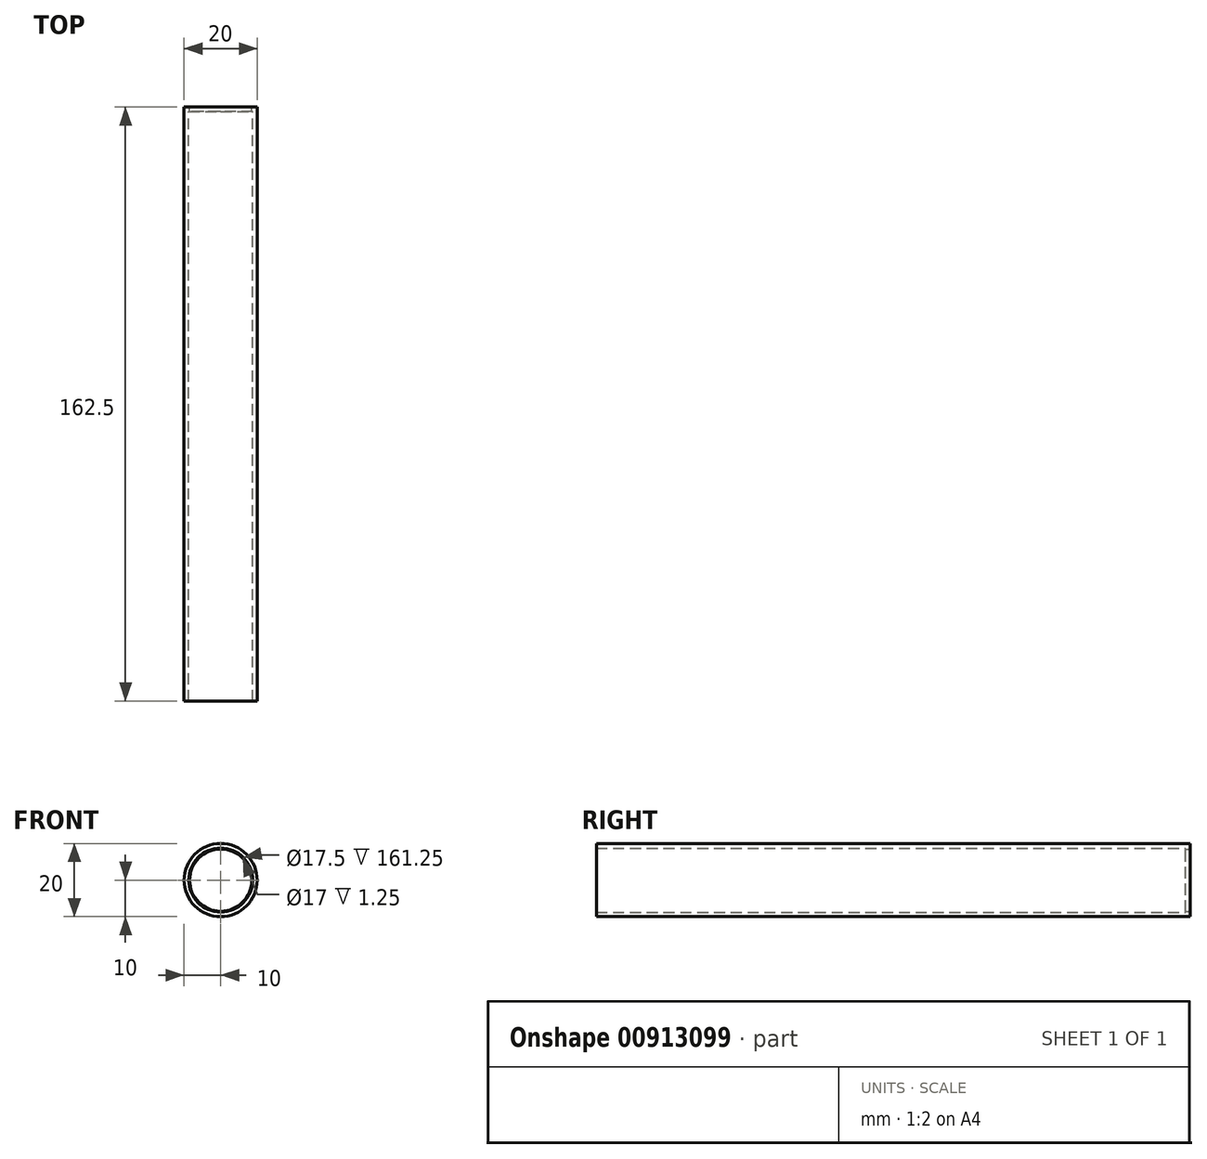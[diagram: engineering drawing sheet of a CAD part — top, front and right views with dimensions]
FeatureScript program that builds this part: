
annotation { "Feature Type Name" : "Feature", "Feature Type Description" : "" }
export const myFeature = defineFeature(function(context is Context, id is Id, definition is map)
    precondition{}
    {
        {
            var Q0;
            Q0=qCreatedBy(makeId("Front.planeOp"),FACE);
            var sketch = newSketch(context, id + "F0", { "sketchPlane" : qUnion([Q0])});
            skCircle(sketch, "E0", {"center": v(0, 0) * mm, "radius": 10 * mm});
            skSolve(sketch);
        }
        {
            var Q0;
            Q0=makeQuery(id+"F0.imprint","IMPRINT",FACE,{"disambiguationData":[TD([[makeQuery(id+"F0.imprint","IMPRINT",EDGE,{"derivedFrom":sQuery(id+"F0.wireOp",EDGE,"E0")}),1.0]])]});
            extrude(context, id + "F1", {"entities" : qUnion([Q0]), "depth" : 162.5 * mm, "offsetDistance" : 25 * mm});
        }
        {
            var Q0;
            Q0=makeQuery(id+"F1.opExtrude","CAP_FACE",FACE,{"disambiguationData":[OSD([sQuery(id+"F0.wireOp",EDGE,"E0")])],"isStart":false});
            var Q1;
            Q1=makeQuery(id+"F1.opExtrude","SWEPT_BODY",BODY,{"disambiguationData":[OSD([sQuery(id+"F0.wireOp",EDGE,"E0")])]});
            shell(context, id + "F2", {"entities" : qUnion([Q0]), "parts" : qUnion([Q1]), "thickness" : 1.25 * mm});
        }
        {
            var Q0;
            Q0=sQuery(id+"F0.wireOp",VERTEX,"E0.center");
            var Q1;
            Q1=makeQuery(id+"F1.opExtrude","SWEPT_BODY",BODY,{"disambiguationData":[OSD([sQuery(id+"F0.wireOp",EDGE,"E0")])]});
            hole(context, id + "F3", {"style" : HoleStyle.SIMPLE, "endStyle" : HoleEndStyle.THROUGH, "oppositeDirection" : true, "holeDiameter" : 17 * mm, "majorDiameter" : 5 * mm, "isTappedThrough" : true, "tappedDepth" : 12 * mm, "tapClearance" : 3, "locations" : qUnion([Q0]), "scope" : qUnion([Q1])});
        }
    });
